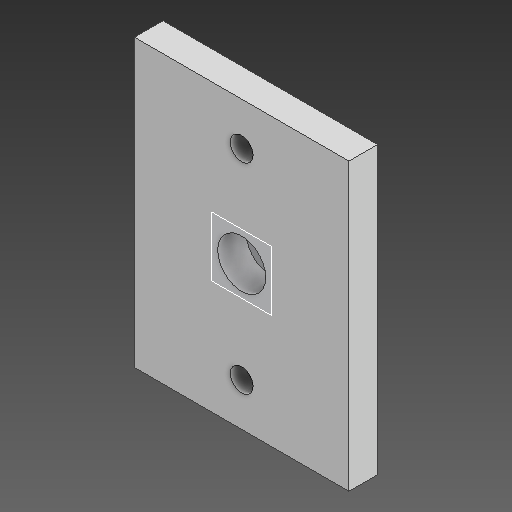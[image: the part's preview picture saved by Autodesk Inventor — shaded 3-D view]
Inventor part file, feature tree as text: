
AUTODESK INVENTOR PART (.ipt)
format: ipt  version: 2021 (Build 250183000, 183)  size: 96,256 bytes
history: native  units: in
note: dims shown in document units (in); Inventor stores cm internally (conversion verified against a paired STEP export)
features: other x3, sketch x1, plane x1
ambient origin geometry x8: Origin, YZ Plane, XZ Plane, XY Plane, X Axis, Y Axis, Z Axis, Center Point
bodies: Solid1 (feature_tree)
feature tree (5):
  other  "Soporte Pistón.ipt"
  other  "Solid1::Soporte Pistón.ipt"
  other  "TaggingFeature1"
  sketch  "Sketch1"  dims[d0=0.3937in]
  plane  "Work Plane1"
